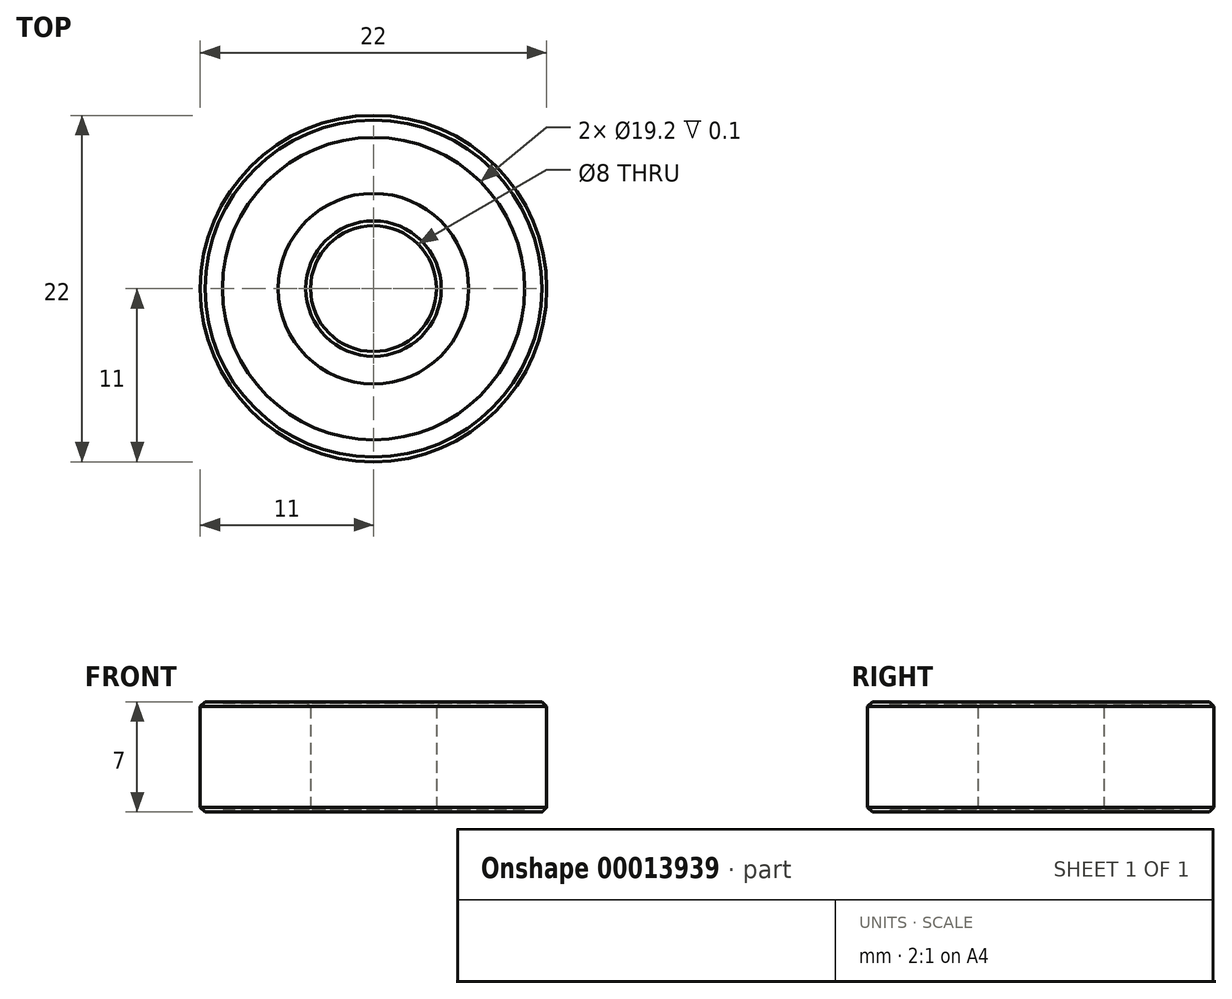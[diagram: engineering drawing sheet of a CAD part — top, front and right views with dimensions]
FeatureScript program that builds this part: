
annotation { "Feature Type Name" : "Feature", "Feature Type Description" : "" }
export const myFeature = defineFeature(function(context is Context, id is Id, definition is map)
    precondition{}
    {
        {
            var Q0;
            Q0=qCreatedBy(makeId("Top.planeOp"),FACE);
            var sketch = newSketch(context, id + "F0", { "sketchPlane" : qUnion([Q0])});
            skCircle(sketch, "E0", {"center": v(0, 0) * mm, "radius": 11 * mm});
            skCircle(sketch, "E1", {"center": v(0, 0) * mm, "radius": 9.6 * mm});
            skCircle(sketch, "E2", {"center": v(0, 0) * mm, "radius": 6.05 * mm});
            skCircle(sketch, "E3", {"center": v(0, 0) * mm, "radius": 4 * mm});
            skSolve(sketch);
        }
        {
            var Q0;
            Q0=makeQuery(id+"F0.imprint","IMPRINT",FACE,{"disambiguationData":[TD([[makeQuery(id+"F0.imprint","IMPRINT",EDGE,{"derivedFrom":sQuery(id+"F0.wireOp",EDGE,"E0")}),1.0]])]});
            var Q1;
            Q1=makeQuery(id+"F0.imprint","IMPRINT",FACE,{"disambiguationData":[TD([[makeQuery(id+"F0.imprint","IMPRINT",EDGE,{"derivedFrom":sQuery(id+"F0.wireOp",EDGE,"E2")}),1.0]])]});
            var Q2;
            Q2=makeQuery(id+"F0.imprint","IMPRINT",FACE,{"disambiguationData":[TD([[makeQuery(id+"F0.imprint","IMPRINT",EDGE,{"derivedFrom":sQuery(id+"F0.wireOp",EDGE,"E1")}),1.0]])]});
            extrude(context, id + "F1", {"entities" : qUnion([Q0, Q1, Q2]), "depth" : 7 * mm});
        }
        {
            var Q0;
            Q0=makeQuery(id+"F0.imprint","IMPRINT",FACE,{"disambiguationData":[TD([[makeQuery(id+"F0.imprint","IMPRINT",EDGE,{"derivedFrom":sQuery(id+"F0.wireOp",EDGE,"E1")}),1.0]])]});
            extrude(context, id + "F2", {"entities" : qUnion([Q0]), "operationType" : NewBodyOperationType.REMOVE, "depth" : 0.1 * mm});
        }
        {
            var Q0;
            Q0=makeQuery(id+"F1.opExtrude","CAP_FACE",FACE,{"disambiguationData":[OSD([sQuery(id+"F0.wireOp",EDGE,"E0"),sQuery(id+"F0.wireOp",EDGE,"E3")])],"isStart":false});
            var sketch = newSketch(context, id + "F3", { "sketchPlane" : qUnion([Q0])});
            skCircle(sketch, "E4.0", {"center": v(0, 0) * mm, "radius": 6.05 * mm});
            skCircle(sketch, "E5.0", {"center": v(0, 0) * mm, "radius": 9.6 * mm});
            skSolve(sketch);
        }
        {
            var Q0;
            Q0=makeQuery(id+"F3.imprint","IMPRINT",FACE,{"disambiguationData":[TD([[makeQuery(id+"F3.imprint","IMPRINT",EDGE,{"derivedFrom":sQuery(id+"F3.wireOp",EDGE,"E4.0")}),-1.0]])]});
            extrude(context, id + "F4", {"entities" : qUnion([Q0]), "operationType" : NewBodyOperationType.REMOVE, "oppositeDirection" : true, "depth" : 0.1 * mm});
        }
        {
            var Q0;
            Q0=makeQuery(id+"F1.opExtrude","CAP_EDGE",EDGE,{"disambiguationData":[OSD([sQuery(id+"F0.wireOp",EDGE,"E0")])],"isStart":false});
            var Q1;
            Q1=makeQuery(id+"F1.opExtrude","CAP_EDGE",EDGE,{"disambiguationData":[OSD([sQuery(id+"F0.wireOp",EDGE,"E0")])],"isStart":true});
            var Q2;
            Q2=makeQuery(id+"F1.opExtrude","CAP_EDGE",EDGE,{"disambiguationData":[OSD([sQuery(id+"F0.wireOp",EDGE,"E3")])],"isStart":false});
            var Q3;
            Q3=makeQuery(id+"F1.opExtrude","CAP_EDGE",EDGE,{"disambiguationData":[OSD([sQuery(id+"F0.wireOp",EDGE,"E3")])],"isStart":true});
            chamfer(context, id + "F5", {"entities" : qUnion([Q0, Q1, Q2, Q3]), "width" : 0.3 * mm, "tangentPropagation" : true});
        }
    });
